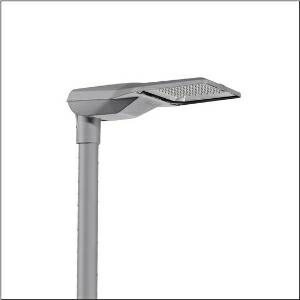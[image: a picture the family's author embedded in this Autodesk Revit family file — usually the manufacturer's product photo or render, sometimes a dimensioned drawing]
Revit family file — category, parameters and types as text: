
# Revit family: streetlight_sl_21_iq_midi___pc-l_5xe3f41g08mb_febf
name_source: partatom
category: Lighting Fixtures
units: mm (PartAtom-declared; Revit-internal decimal feet)

## family parameters
Cut with Voids When Loaded = No
Host = Face
Light Source = No
Part Type = Normal
Room Calculation Point = No
Round Connector Dimension = Use Diameter
Shared = No

## types (1)
- --- (1 x LED, 19370 lm, 146.7 W, 4000K)
    Apparent Load = 147 VA
    CIE Flux Codes = 38 78 98 100 100
    Color Rendering = 70
    Color Temperature = 4000K
    Default Elevation = 1800 mm
    Description = Streetlight SL 21 iQ midi, mast luminaire, primary light control with lens, of PMMA, primary optical cover: cover, of toughened safety glass, transparent, light distribution: PC-L, light emission: direct distribution, primary light characteristic: asymmetric, left, installation type: post-top, side-entry, LED, High Power LED, rated luminous flux: 19.370lm, luminous efficacy: 132lm/W, light colour: 740, colour temperature: 4000K, control gear: iQ Street-Remote, control: Street-Remote, Auto-Match, Temp-Guard, Lumen-Switch, Night-Set, Smart-Wire, Light-Fading, Desk-Remote (wireless, voltage-free reading and setting of iQ features in the workshop via application-optimized NFC function/RFID function), optimised constant luminous flux control (CLO 2.0), pre-setting: linear dimming characteristic, mains connection: 230..240V, AC, 50/60Hz, start of lifetime: 147W, end of service life: 161W, reduction: 62W, luminaire housing, of diecast aluminium, powder-coated, SITECO metallic grey (DB 702S), corrosivity category C5 high according to DIN EN ISO 12944, please order mast flange separately, inclination adjustable: 0°, 5°, 10°, 15°, sealing non-destructively replaceable, multi-level sealing system, length: 644mm, width: 335mm, height: 110mm, mast flange for spigot size: 42mm (side-entry): 5XC10008XM4, 60/48mm (side-entry/post-top): 5XC10108XM2, 76/60mm (side-entry/post-top): 5XC10108XM1, mounting height: 4..8m, protection rating (complete): IP66, insulation class (complete): insulation class II (safety insulation), certification: CE, ENEC, ENEC+, VDE, impact resistance: IK10, permissible operating ambient temperature for outdoor applications: -40..+50°C, standard-compliant lighting for roads and squares, packaging unit: 1 piece

Light Distribution: PC-L
    Height = 111 mm
    Lamp = 1 x LED
    Lamp Light Flux = 19370 lm
    Lamp Power = 146.7 W
    Lamp count = 1
    Length = 644 mm
    Luminous efficacy = 132 lm/W
    Manufacturer = Siteco
    ModVariant = No
    Model = 5XE3F41G08MB
    Number of Poles = 1
    OnlyDefault = Yes
    Power Factor = 1
    Product Name = Streetlight SL 21 iQ midi | PC-L
    Product group = mast luminaire | pylon top
    ProductGroupID = 6100
    Protection Class = Protection class II
    Protection Degree = IP 66
    RLX_Detail_Level = 1
    RLX_Emergency_Light_Flux = 0 lm
    RLX_Emergency_Type = 0
    RLX_Emergency_Type_DB = No
    RlxData = <blob elided: 29569 chars, md5=98342c5e>
    Socket = socket
    Standby Power = 0 W
    System Light Flux = 19370 lm
    System Power = 147 W
    Type Comments = factory setting: luminous flux: 100 % | dim-lin: 254 | 753 mA
    Type Image = l_1004298.jpg
    URL = http://relux.com
    VarID = @adj_072041
    Voltage = 0 V
    Weight = 0.00 kg
    Width = 336 mm

## geometry (parser evidence)
native form markers: Blend x4, Sweep x10
no freeform markers — native parametric forms only
